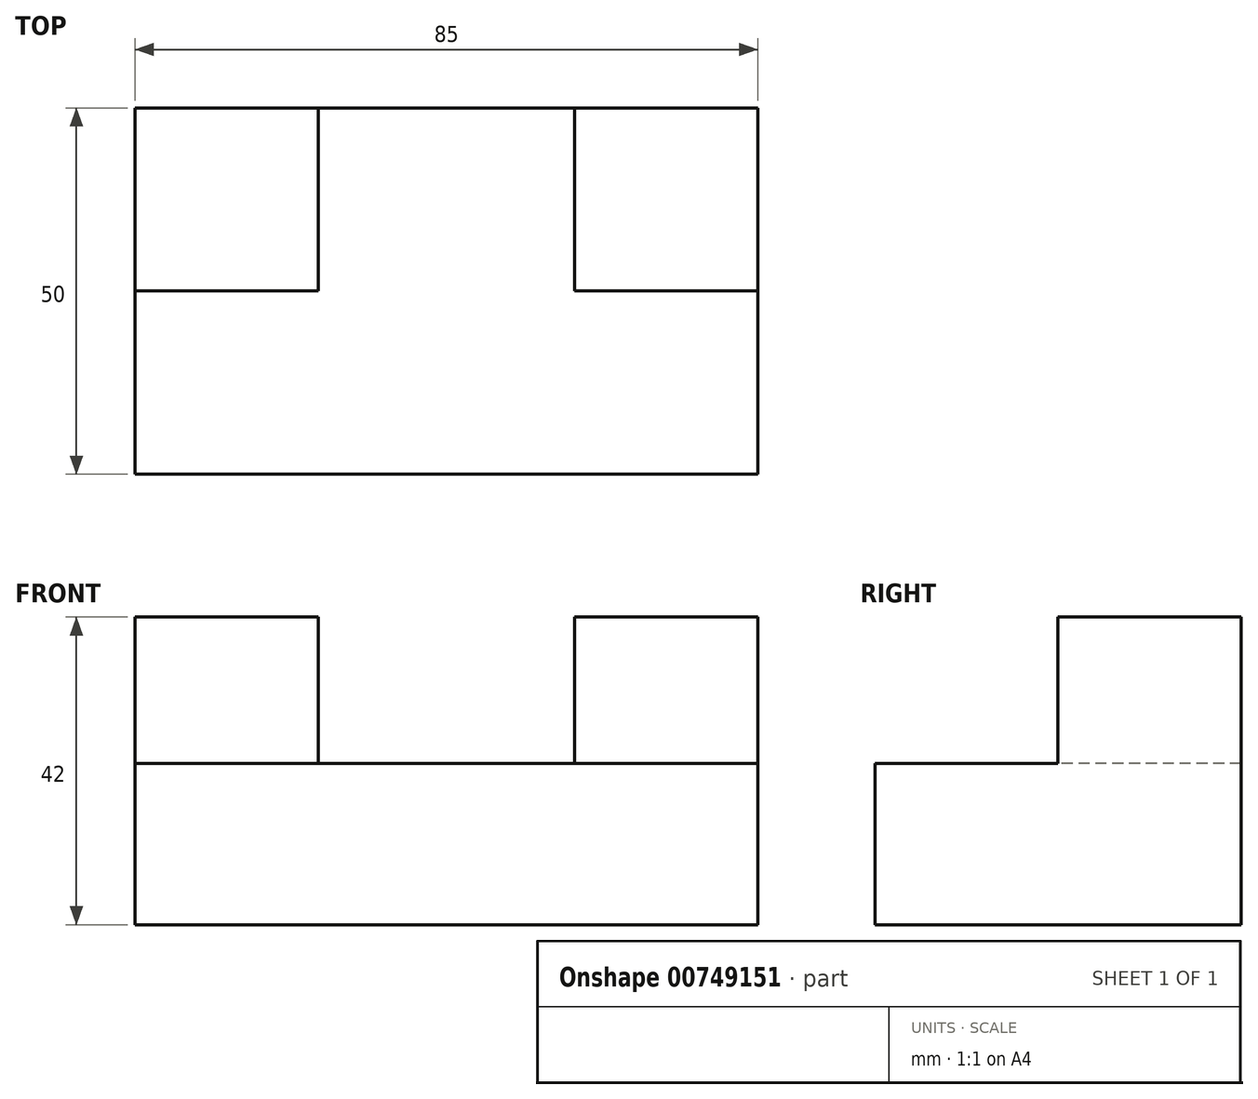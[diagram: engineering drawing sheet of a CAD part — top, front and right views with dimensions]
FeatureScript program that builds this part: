
annotation { "Feature Type Name" : "Feature", "Feature Type Description" : "" }
export const myFeature = defineFeature(function(context is Context, id is Id, definition is map)
    precondition{}
    {
        {
            var Q0;
            Q0=qCreatedBy(makeId("Top.planeOp"),FACE);
            var sketch = newSketch(context, id + "F0", { "sketchPlane" : qUnion([Q0])});
            skLineSegment(sketch, "E0.bottom", {"start": v(-42.5, 25) * mm, "end": v(42.5, 25) * mm});
            skLineSegment(sketch, "E0.top", {"start": v(-42.5, -25) * mm, "end": v(42.5, -25) * mm});
            skLineSegment(sketch, "E0.left", {"start": v(-42.5, 25) * mm, "end": v(-42.5, -25) * mm});
            skLineSegment(sketch, "E0.right", {"start": v(42.5, 25) * mm, "end": v(42.5, -25) * mm});
            skPoint(sketch, "E0.middle", {"position": v(0, 0) * mm});
            skLineSegment(sketch, "E1.bottom", {"start": v(-42.5, 25) * mm, "end": v(-17.5, 25) * mm});
            skLineSegment(sketch, "E1.top", {"start": v(-42.5, 0) * mm, "end": v(-17.5, 0) * mm});
            skLineSegment(sketch, "E1.left", {"start": v(-42.5, 25) * mm, "end": v(-42.5, 0) * mm});
            skLineSegment(sketch, "E1.right", {"start": v(-17.5, 25) * mm, "end": v(-17.5, 0) * mm});
            skLineSegment(sketch, "E2.bottom", {"start": v(42.5, 25) * mm, "end": v(17.5, 25) * mm});
            skLineSegment(sketch, "E2.top", {"start": v(42.5, 0) * mm, "end": v(17.5, 0) * mm});
            skLineSegment(sketch, "E2.left", {"start": v(42.5, 25) * mm, "end": v(42.5, 0) * mm});
            skLineSegment(sketch, "E2.right", {"start": v(17.5, 25) * mm, "end": v(17.5, 0) * mm});
            skSolve(sketch);
        }
        {
            var Q0;
            {var subQ1=sQuery(id+"F0.wireOp",EDGE,"E0.top");Q0=makeQuery(id+"F0.imprint","IMPRINT",FACE,{"disambiguationData":[TD([[makeQuery(id+"F0.imprint","IMPRINT",EDGE,{"derivedFrom":subQ1}),1.0]])]});}
            extrude(context, id + "F1", {"entities" : qUnion([Q0]), "depth" : 22 * mm, "offsetDistance" : 25 * mm});
        }
        {
            var Q0;
            {var subQ4=sQuery(id+"F0.wireOp",EDGE,"E1.top");Q0=makeQuery(id+"F0.imprint","IMPRINT",FACE,{"disambiguationData":[TD([[makeQuery(id+"F0.imprint","IMPRINT",EDGE,{"derivedFrom":subQ4}),1.0]])]});}
            var Q1;
            {var subQ4=sQuery(id+"F0.wireOp",EDGE,"E2.top");Q1=makeQuery(id+"F0.imprint","IMPRINT",FACE,{"disambiguationData":[TD([[makeQuery(id+"F0.imprint","IMPRINT",EDGE,{"derivedFrom":subQ4}),-1.0]])]});}
            extrude(context, id + "F2", {"entities" : qUnion([Q0, Q1]), "operationType" : NewBodyOperationType.ADD, "depth" : 42 * mm, "offsetDistance" : 25 * mm});
        }
    });
